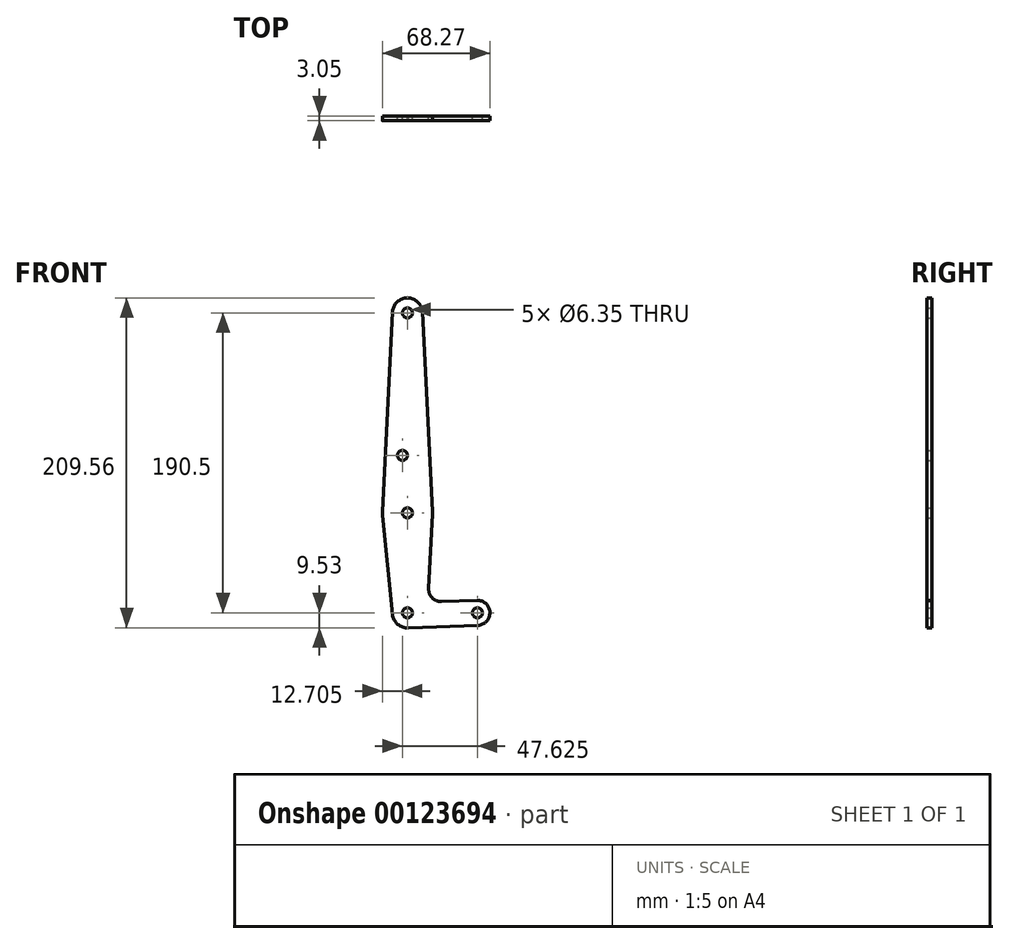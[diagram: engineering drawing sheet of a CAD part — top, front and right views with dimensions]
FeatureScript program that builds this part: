
annotation { "Feature Type Name" : "Feature", "Feature Type Description" : "" }
export const myFeature = defineFeature(function(context is Context, id is Id, definition is map)
    precondition{}
    {
        {
            var Q0;
            Q0=qCreatedBy(makeId("Front.planeOp"),FACE);
            var sketch = newSketch(context, id + "F0", { "sketchPlane" : qUnion([Q0])});
            skLineSegment(sketch, "E0", {"start": v(0, 0) * mm, "end": v(0, 63.5) * mm, "construction": true});
            skLineSegment(sketch, "E1", {"start": v(0, 63.5) * mm, "end": v(0, 190.5) * mm, "construction": true});
            skLineSegment(sketch, "E2", {"start": v(0, 0) * mm, "end": v(44.45, 0) * mm, "construction": true});
            skCircle(sketch, "E3", {"center": v(0, 190.5) * mm, "radius": 9.52 * mm});
            skCircle(sketch, "E4", {"center": v(0, 63.5) * mm, "radius": 15.88 * mm});
            skCircle(sketch, "E5", {"center": v(0, 0) * mm, "radius": 9.53 * mm});
            skCircle(sketch, "E6", {"center": v(44.45, 0) * mm, "radius": 7.94 * mm});
            skLineSegment(sketch, "E7", {"start": v(-9.51, 190.98) * mm, "end": v(-15.86, 64.3) * mm});
            skLineSegment(sketch, "E8", {"start": v(9.51, 190.98) * mm, "end": v(15.86, 64.3) * mm});
            skLineSegment(sketch, "E9", {"start": v(0, -9.52) * mm, "end": v(44.73, -7.93) * mm});
            skLineSegment(sketch, "E10", {"start": v(21.71, 7.13) * mm, "end": v(44.17, 7.93) * mm});
            skCircle(sketch, "E11", {"center": v(0, 190.5) * mm, "radius": 3.18 * mm});
            skCircle(sketch, "E12", {"center": v(0, 63.5) * mm, "radius": 3.18 * mm});
            skCircle(sketch, "E13", {"center": v(0, 0) * mm, "radius": 3.18 * mm});
            skCircle(sketch, "E14", {"center": v(44.45, 0) * mm, "radius": 3.18 * mm});
            skCircle(sketch, "E15", {"center": v(-3.18, 100.03) * mm, "radius": 3.18 * mm});
            skArc(sketch, "E16.filletArc", {"start": v(13.52, 15.87) * mm, "mid": v(15.63, 9.64) * mm, "end": v(21.71, 7.13) * mm});
            skLineSegment(sketch, "E17", {"start": v(-15.8, 61.91) * mm, "end": v(-9.48, -0.95) * mm});
            skLineSegment(sketch, "E18", {"start": v(15.86, 62.7) * mm, "end": v(13.5, 15.48) * mm});
            skSolve(sketch);
        }
        {
            var Q0;
            Q0 = qSketchRegion(id + "F0", true);
            extrude(context, id + "F1", {"entities" : qUnion([Q0]), "depth" : 3.05 * mm});
        }
    });
